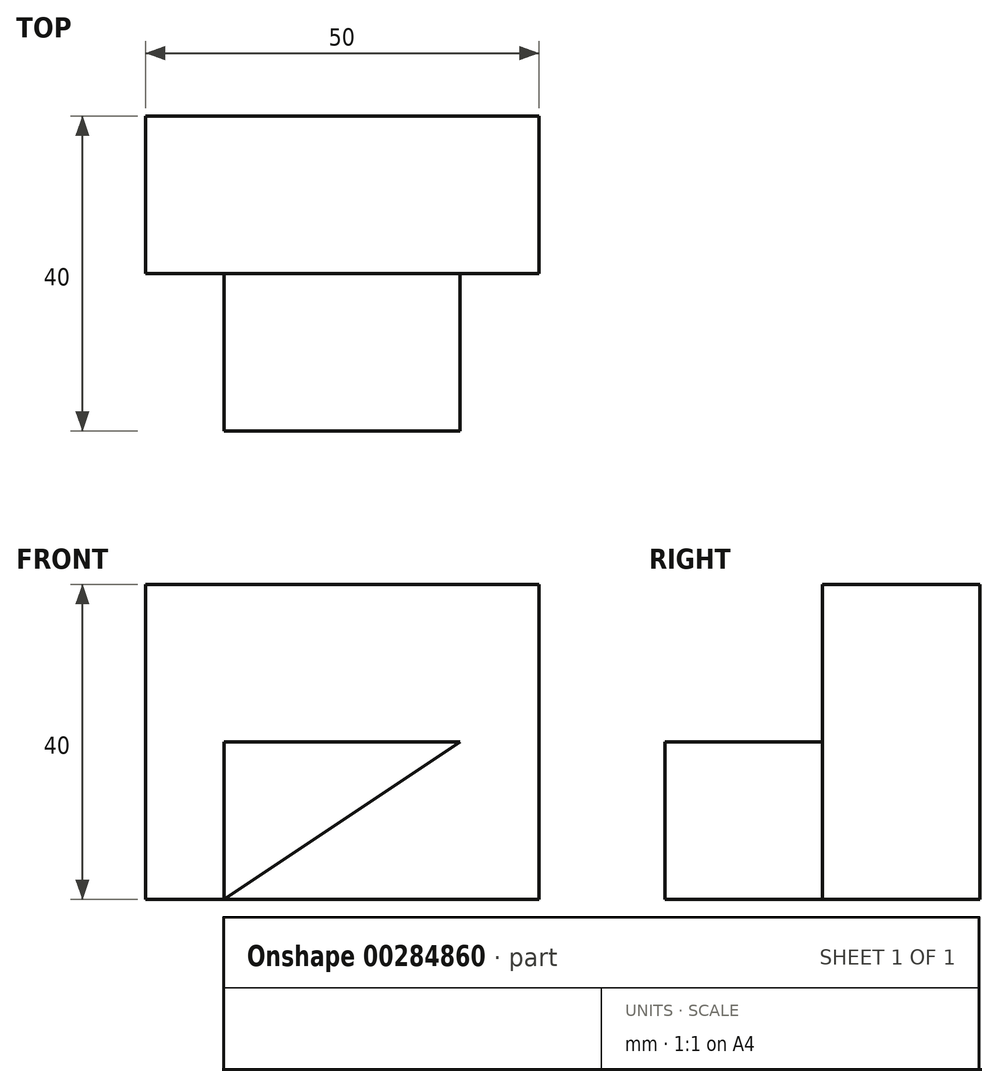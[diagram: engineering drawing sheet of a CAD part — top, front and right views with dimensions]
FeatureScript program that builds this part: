
annotation { "Feature Type Name" : "Feature", "Feature Type Description" : "" }
export const myFeature = defineFeature(function(context is Context, id is Id, definition is map)
    precondition{}
    {
        {
            var Q0;
            Q0=qCreatedBy(makeId("Front.planeOp"),FACE);
            var sketch = newSketch(context, id + "F0", { "sketchPlane" : qUnion([Q0])});
            skLineSegment(sketch, "E0.bottom", {"start": v(0, 0) * mm, "end": v(50, 0) * mm});
            skLineSegment(sketch, "E0.top", {"start": v(0, 40) * mm, "end": v(50, 40) * mm});
            skLineSegment(sketch, "E0.left", {"start": v(0, 0) * mm, "end": v(0, 40) * mm});
            skLineSegment(sketch, "E0.right", {"start": v(50, 0) * mm, "end": v(50, 40) * mm});
            skSolve(sketch);
        }
        {
            var Q0;
            Q0=qSketchRegion(id+"F0",true);
            extrude(context, id + "F1", {"entities" : qUnion([Q0]), "depth" : 20 * mm});
        }
        {
            var Q0;
            Q0=makeQuery(id+"F1.opExtrude","CAP_FACE",FACE,{"disambiguationData":[OSD([sQuery(id+"F0.wireOp",EDGE,"E0.bottom"),sQuery(id+"F0.wireOp",EDGE,"E0.top"),sQuery(id+"F0.wireOp",EDGE,"E0.left"),sQuery(id+"F0.wireOp",EDGE,"E0.right")])],"isStart":false});
            var sketch = newSketch(context, id + "F2", { "sketchPlane" : qUnion([Q0])});
            skLineSegment(sketch, "E1.bottom", {"start": v(10, 0) * mm, "end": v(40, 0) * mm});
            skLineSegment(sketch, "E1.top", {"start": v(10, 20) * mm, "end": v(40, 20) * mm});
            skLineSegment(sketch, "E1.left", {"start": v(10, 0) * mm, "end": v(10, 20) * mm});
            skLineSegment(sketch, "E1.right", {"start": v(40, 0) * mm, "end": v(40, 20) * mm});
            skLineSegment(sketch, "E2", {"start": v(40, 20) * mm, "end": v(10, 0) * mm});
            skSolve(sketch);
        }
        {
            var Q0;
            Q0=makeQuery(id+"F2.imprint","IMPRINT",FACE,{"disambiguationData":[TD([[makeQuery(id+"F2.imprint","IMPRINT",EDGE,{"derivedFrom":sQuery(id+"F2.wireOp",EDGE,"E1.top")}),-1.0]])]});
            extrude(context, id + "F3", {"entities" : qUnion([Q0]), "operationType" : NewBodyOperationType.ADD, "depth" : 20 * mm});
        }
    });
